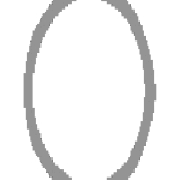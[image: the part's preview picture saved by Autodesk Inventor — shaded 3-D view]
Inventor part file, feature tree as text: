
AUTODESK INVENTOR PART (.ipt)
format: ipt  version: 2021 (Build 250183000, 183)  size: 110,592 bytes
history: native  units: in
note: dims shown in document units (in); Inventor stores cm internally (conversion verified against a paired STEP export)
features: other x4, sketch x3, plane x1
ambient origin geometry x8: Origin, YZ Plane, XZ Plane, XY Plane, X Axis, Y Axis, Z Axis, Center Point
bodies: Solid1 (feature_tree), Body (feature_tree)
feature tree (8):
  other  "Driven Length"
  other  "Frame Generator"
  other  "Start Plane"
  other  "End Plane"
  sketch  "Sketch"  dims[d2=9.0139in d4=-0.0in d5=9.0139in d6=0.12in d7=0.0in d8=90.0deg d9=9.0139in]
  sketch  "Sketch2"  dims[d0=1.0in]
  plane  "Work Plane3"
  sketch  "Sketch3"  dims[d1=0.065in]
